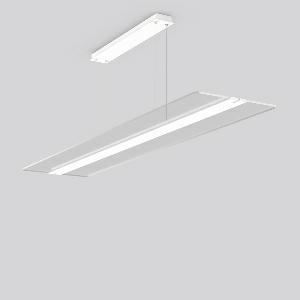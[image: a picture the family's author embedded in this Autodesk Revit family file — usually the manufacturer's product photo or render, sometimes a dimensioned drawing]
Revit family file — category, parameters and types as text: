
# Revit family: twindot_s_312265_002_730_0446
name_source: partatom
category: Lighting Fixtures
units: mm (PartAtom-declared; Revit-internal decimal feet)

## family parameters
Cut with Voids When Loaded = No
Host = Face
Light Source = No
Part Type = Normal
Room Calculation Point = No
Round Connector Dimension = Use Diameter
Shared = No

## types (1)
- TWINDOT S (1 x LED Modul 830, 8100 lm, 3000)
    Apparent Load = 65 VA
    CIE Flux Codes = 47 77 94 55 100
    Color Rendering = 80
    Color Temperature = 3000
    Default Elevation = 1800 mm
    Description = Series: TWINDOT S
LED pendant luminaire with extremely flat and frameless appearance. Middle bar made of aluminium extrusion profile, powder-coated. Transparent light guide made of UV-resistant acrylic glass (PMMA) with TWINDOT prismatic. Light control with perfectly glare-free TWINDOT technology for pleasantly gentle light with soft shadows. Even and wide indirect and direct light distribution. Direct 55%, indirect 45% light emission. 4-point steel cable suspension, steplessly adjustable. Converter integrated in the canopy (powder-coated white). Power supply through suspension cable. 
Colour: traffic white, matt (RAL 9016)
Length: 1500 mm
Width: 350 mm
Height: 20 mm
Suspension length: 500-1200 mm
Lamp: LED
Socket: without socket
Colour temperature: 3000K
Colour rendering index (CRI): 80
System power: 65 W
Rated luminous flux: 8100 lm
Luminous efficiency: 125 lm/W
Control gear: Dimmable Bluetooth converter
Protection class: I
Type of protection: IP 20
    Height = 20 mm  [stored 0.0656168 ft]
    Lamp = 1 x LED Modul 830
    Lamp Light Flux = 8100 lm
    Lamp count = 1
    Length = 1500 mm
    Lifetime = 50000 h
    Luminous efficacy = 125 lm/W
    Manufacturer = RZB
    ModVariant = No
    Model = 312265.002.730
    Mounting Place = Ceiling
    Mounting Type = Pendant
    Number of Poles = 1
    OnlyDefault = Yes
    Power Factor = 1
    Product Name = TWINDOT S
    Product group = Pendant modular luminaires
    ProductGroupID = 906
    Protection Class = Protection class I
    Protection Degree = IP 20
    RLX_Detail_Level = 1
    RLX_Emergency_Light_Flux = 0 lm
    RLX_Emergency_Type = 0
    RLX_Emergency_Type_DB = No
    RlxData = <blob elided: 36657 chars, md5=7cd59c1e>
    Socket = socket
    Standby Power = 0 W
    System Light Flux = 8100 lm
    System Power = 65 W
    Type Comments = Product without accessories
    Type Image = 312265.002.jpg
    URL = http://relux.com
    VarID = ---
    Voltage = 230 V
    Voltage Range = 220-240 V
    Weight = 0.00 kg
    Width = 350 mm

note: [stored X ft] marks values corroborated as IEEE doubles in the binary element streams (Revit-internal decimal feet)

## geometry (parser evidence)
native form markers: Blend x4, Sweep x12
no freeform markers — native parametric forms only
